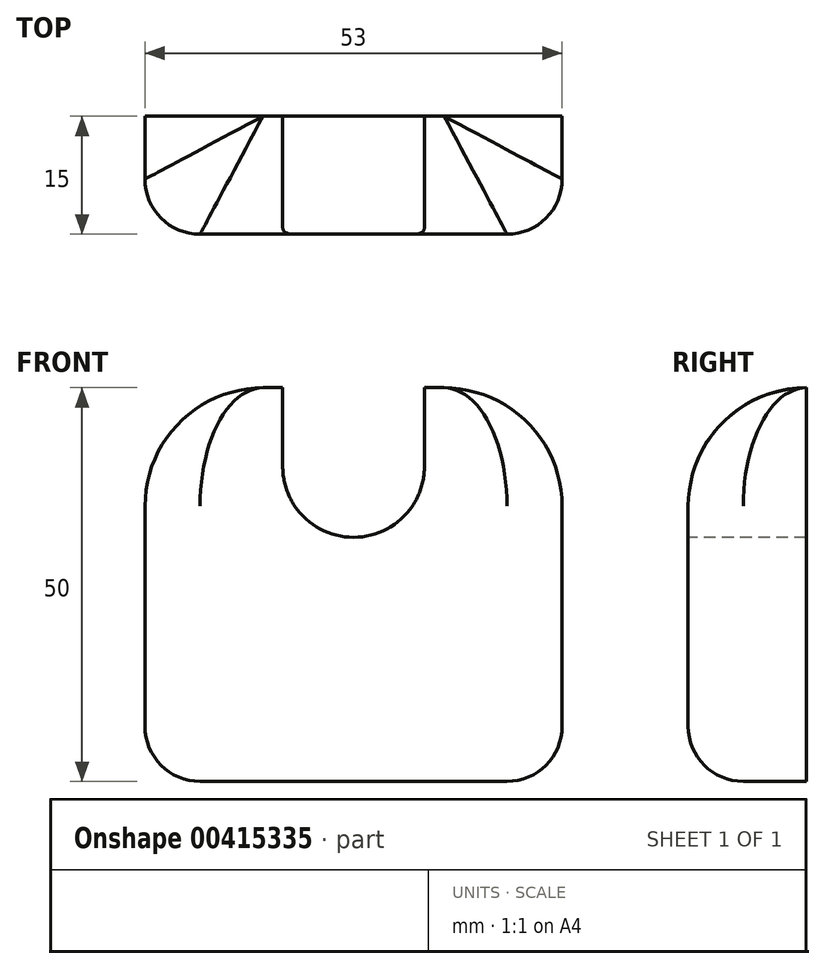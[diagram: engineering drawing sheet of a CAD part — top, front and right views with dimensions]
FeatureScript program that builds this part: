
annotation { "Feature Type Name" : "Feature", "Feature Type Description" : "" }
export const myFeature = defineFeature(function(context is Context, id is Id, definition is map)
    precondition{}
    {
        {
            var Q0;
            Q0=qCreatedBy(makeId("Front.planeOp"),FACE);
            var sketch = newSketch(context, id + "F0", { "sketchPlane" : qUnion([Q0])});
            skLineSegment(sketch, "E0.bottom", {"start": v(0, 0) * mm, "end": v(53, 0) * mm});
            skLineSegment(sketch, "E0.top", {"start": v(0, 50) * mm, "end": v(53, 50) * mm});
            skLineSegment(sketch, "E0.left", {"start": v(0, 0) * mm, "end": v(0, 50) * mm});
            skLineSegment(sketch, "E0.right", {"start": v(53, 0) * mm, "end": v(53, 50) * mm});
            skSolve(sketch);
        }
        {
            var Q0;
            Q0 = qSketchRegion(id + "F0", true);
            extrude(context, id + "F1", {"entities" : qUnion([Q0]), "depth" : 15 * mm});
        }
        {
            var Q0;
            Q0=makeQuery(id+"F1.opExtrude","CAP_FACE",FACE,{"disambiguationData":[OSD([sQuery(id+"F0.wireOp",EDGE,"E0.bottom"),sQuery(id+"F0.wireOp",EDGE,"E0.top"),sQuery(id+"F0.wireOp",EDGE,"E0.left"),sQuery(id+"F0.wireOp",EDGE,"E0.right")])],"isStart":false});
            var sketch = newSketch(context, id + "F2", { "sketchPlane" : qUnion([Q0])});
            skLineSegment(sketch, "E1", {"start": v(26.5, 50) * mm, "end": v(26.5, 31.06) * mm, "construction": true});
            skLineSegment(sketch, "E2", {"start": v(17.5, 50) * mm, "end": v(17.5, 40) * mm});
            skLineSegment(sketch, "E3", {"start": v(35.5, 50) * mm, "end": v(35.5, 40) * mm});
            skArc(sketch, "E4", {"start": v(17.5, 40) * mm, "mid": v(26.5, 31) * mm, "end": v(35.5, 40) * mm});
            skPoint(sketch, "E5", {"position": v(26.5, 31) * mm});
            skLineSegment(sketch, "E6", {"start": v(17.5, 50) * mm, "end": v(35.5, 50) * mm});
            skSolve(sketch);
        }
        {
            var Q0;
            Q0 = qSketchRegion(id + "F2", true);
            extrude(context, id + "F3", {"entities" : qUnion([Q0]), "operationType" : NewBodyOperationType.REMOVE, "endBound" : BoundingType.UP_TO_NEXT, "oppositeDirection" : true, "depth" : 25.4 * mm});
        }
        {
            var Q0;
            Q0=makeQuery(id+"F1.opExtrude","CAP_EDGE",EDGE,{"disambiguationData":[OSD([sQuery(id+"F0.wireOp",EDGE,"E0.left")])],"isStart":false});
            var Q1;
            Q1=makeQuery(id+"F1.opExtrude","CAP_EDGE",EDGE,{"disambiguationData":[OSD([sQuery(id+"F0.wireOp",EDGE,"E0.right")])],"isStart":false});
            fillet(context, id + "F4", {"entities" : qUnion([Q0, Q1]), "radius" : 7 * mm, "tangentPropagation" : true, "allowEdgeOverflow" : false});
        }
        {
            var Q0;
            Q0=makeQuery(id+"F1.opExtrude","SWEPT_EDGE",EDGE,{"disambiguationData":[OSD([sQuery(id+"F0.wireOp",EDGE,"E0.top"),sQuery(id+"F0.wireOp",EDGE,"E0.left")])]});
            var Q1;
            Q1=makeQuery(id+"F1.opExtrude","SWEPT_EDGE",EDGE,{"disambiguationData":[OSD([sQuery(id+"F0.wireOp",EDGE,"E0.top"),sQuery(id+"F0.wireOp",EDGE,"E0.right")])]});
            fillet(context, id + "F5", {"entities" : qUnion([Q0, Q1]), "radius" : 15 * mm, "tangentPropagation" : true, "allowEdgeOverflow" : false});
        }
        {
            var Q0;
            Q0=makeQuery(id+"F1.opExtrude","CAP_EDGE",EDGE,{"disambiguationData":[OSD([sQuery(id+"F0.wireOp",EDGE,"E0.bottom")])],"isStart":false});
            fillet(context, id + "F6", {"entities" : qUnion([Q0]), "radius" : 7 * mm, "tangentPropagation" : true, "allowEdgeOverflow" : false});
        }
    });
